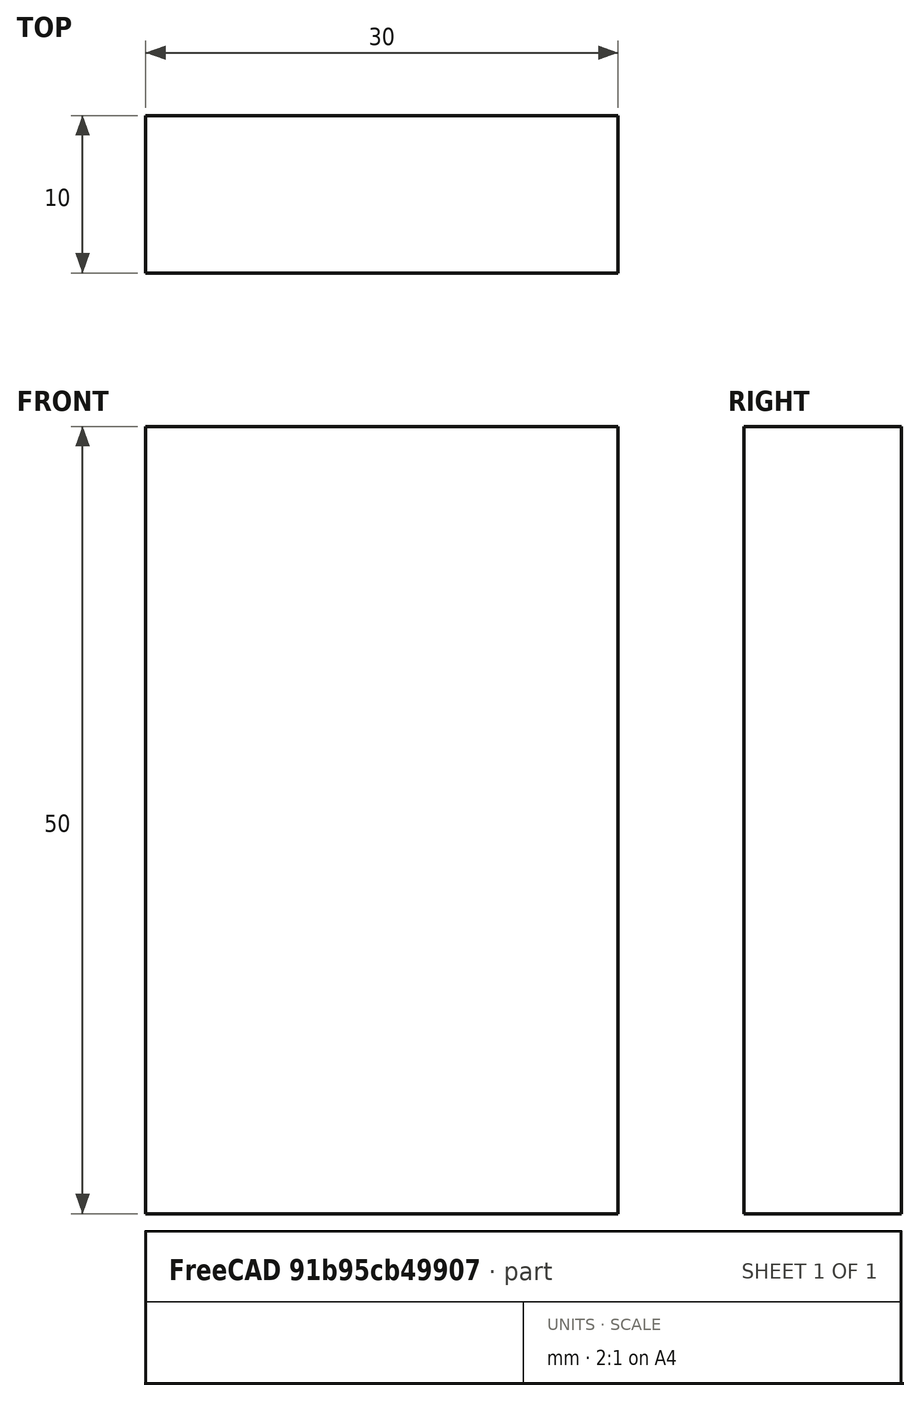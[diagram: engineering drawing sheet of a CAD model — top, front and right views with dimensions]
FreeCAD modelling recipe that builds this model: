
FCSTD DOCUMENT  (FreeCAD 0.15R4671 (Git))
Label: Flat Bar 30x10 EN10058 S235JR
License: All rights reserved
LicenseURL: http://en.wikipedia.org/wiki/All_rights_reserved
objects: Sketcher::SketchObject×1, Part::Extrusion×1
note: 2 computed .brp shape members not serialized (recipe doc carries the construction recipe); baked Part::Feature solids carry a one-line shape summary decoded from their .brp

FEATURE [Sketcher::SketchObject] Sketch
  sketch-geometry (4):
    g0: LineSegment StartX=-15 StartY=-5 StartZ=0 EndX=15 EndY=-5 EndZ=0
    g1: LineSegment StartX=15 StartY=-5 StartZ=0 EndX=15 EndY=5 EndZ=0
    g2: LineSegment StartX=15 StartY=5 StartZ=0 EndX=-15 EndY=5 EndZ=0
    g3: LineSegment StartX=-15 StartY=5 StartZ=0 EndX=-15 EndY=-5 EndZ=0
  constraints (12):
    c: Coincident(g0,g1)
    c: Coincident(g1,g2)
    c: Coincident(g2,g3)
    c: Coincident(g3,g0)
    c: Horizontal(g0)
    c: Horizontal(g2)
    c: Vertical(g1)
    c: Vertical(g3)
    c: Symmetric(g1,g2,g-2)
    c: Symmetric(g0,g1,g-1)
    c: DistanceY(g1) = 10
    c: DistanceX(g0) = 30
FEATURE [Part::Extrusion] Extrude  label="Flat Bar 30x10 EN10058 S235JR"
  Base = -> Sketch
  Dir = (0,0,50)
  Solid = true
